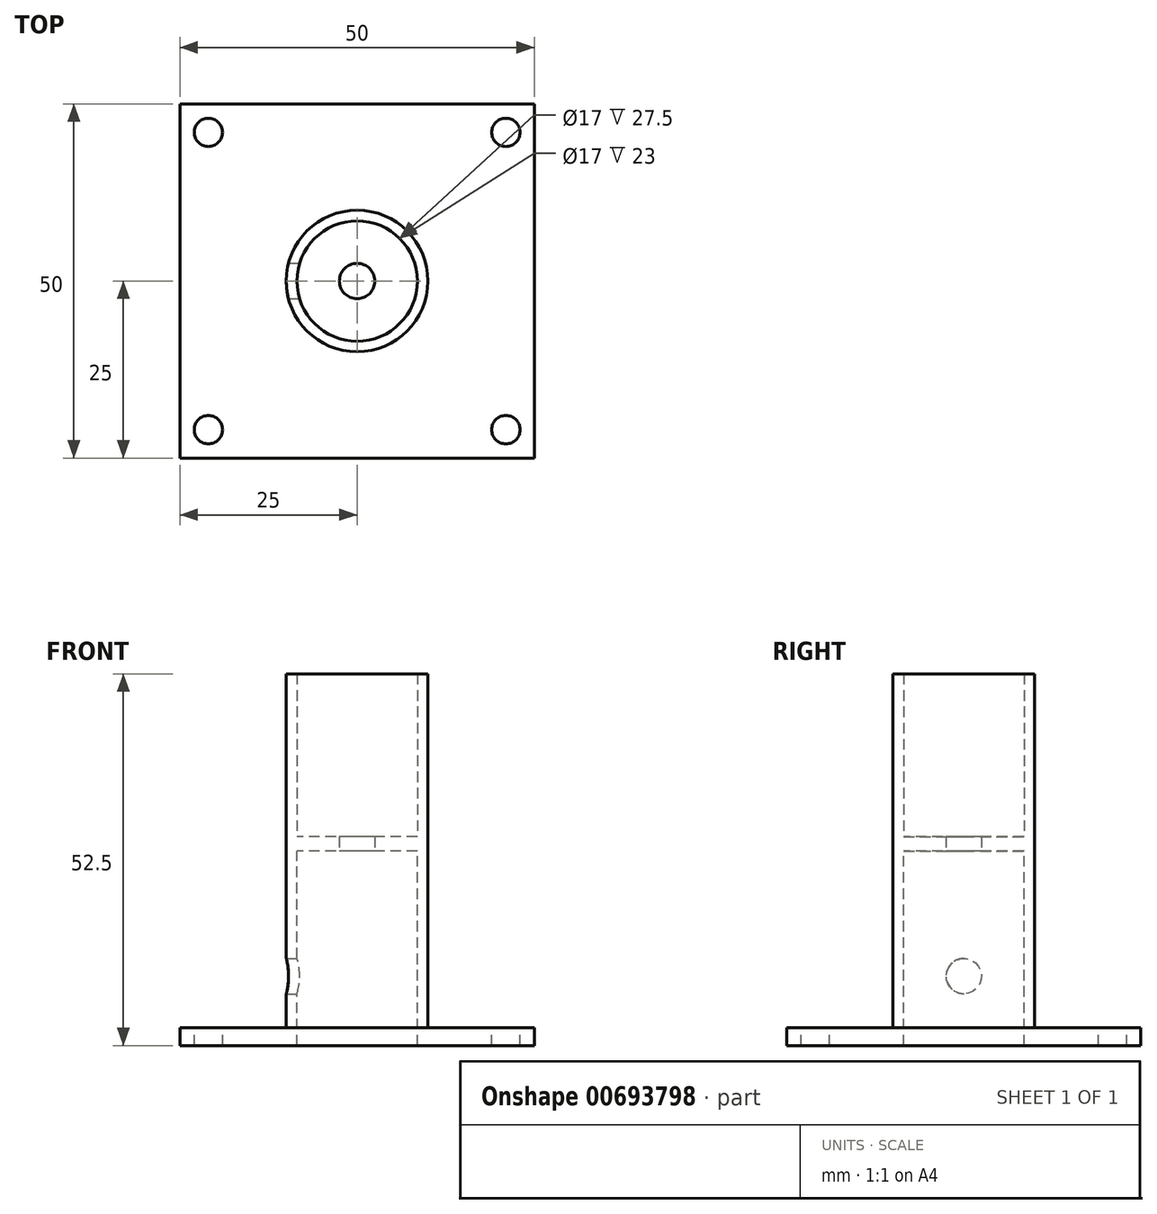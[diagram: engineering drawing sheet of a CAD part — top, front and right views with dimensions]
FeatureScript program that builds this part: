
annotation { "Feature Type Name" : "Feature", "Feature Type Description" : "" }
export const myFeature = defineFeature(function(context is Context, id is Id, definition is map)
    precondition{}
    {
        {
            var Q0;
            Q0=qCreatedBy(makeId("Top.planeOp"),FACE);
            var sketch = newSketch(context, id + "F0", { "sketchPlane" : qUnion([Q0])});
            skLineSegment(sketch, "E0.bottom", {"start": v(-25, 25) * mm, "end": v(25, 25) * mm});
            skLineSegment(sketch, "E0.top", {"start": v(-25, -25) * mm, "end": v(25, -25) * mm});
            skLineSegment(sketch, "E0.left", {"start": v(-25, 25) * mm, "end": v(-25, -25) * mm});
            skLineSegment(sketch, "E0.right", {"start": v(25, 25) * mm, "end": v(25, -25) * mm});
            skPoint(sketch, "E0.middle", {"position": v(0, 0) * mm});
            skCircle(sketch, "E1", {"center": v(0, 0) * mm, "radius": 8.5 * mm});
            skCircle(sketch, "E2", {"center": v(0, 0) * mm, "radius": 10 * mm});
            skLineSegment(sketch, "E3.bottom", {"start": v(21, 21) * mm, "end": v(-21, 21) * mm});
            skLineSegment(sketch, "E3.top", {"start": v(21, -21) * mm, "end": v(-21, -21) * mm});
            skLineSegment(sketch, "E3.left", {"start": v(21, 21) * mm, "end": v(21, -21) * mm});
            skLineSegment(sketch, "E3.right", {"start": v(-21, 21) * mm, "end": v(-21, -21) * mm});
            skCircle(sketch, "E4", {"center": v(-21, 21) * mm, "radius": 2 * mm});
            skCircle(sketch, "E5.MirrorC", {"center": v(21, 21) * mm, "radius": 2 * mm});
            skCircle(sketch, "E6.MirrorC", {"center": v(-21, -21) * mm, "radius": 2 * mm});
            skCircle(sketch, "E7.MirrorC", {"center": v(21, -21) * mm, "radius": 2 * mm});
            skSolve(sketch);
        }
        {
            var Q0;
            Q0 = qSketchRegion(id + "F0", true);
            var Q1;
            Q1=makeQuery(id+"F0.imprint","IMPRINT",FACE,{"disambiguationData":[TD([[makeQuery(id+"F0.imprint","IMPRINT",EDGE,{"derivedFrom":sQuery(id+"F0.wireOp",EDGE,"E2")}),-1.0]])]});
            var Q2;
            Q2=makeQuery(id+"F0.imprint","IMPRINT",FACE,{"disambiguationData":[TD([[makeQuery(id+"F0.imprint","IMPRINT",EDGE,{"derivedFrom":sQuery(id+"F0.wireOp",EDGE,"E1")}),-1.0]])]});
            extrude(context, id + "F1", {"entities" : qUnion([Q0, Q1, Q2]), "oppositeDirection" : true, "depth" : 2.5 * mm, "offsetDistance" : 25 * mm});
        }
        {
            var Q0;
            Q0=makeQuery(id+"F0.imprint","IMPRINT",FACE,{"disambiguationData":[TD([[makeQuery(id+"F0.imprint","IMPRINT",EDGE,{"derivedFrom":sQuery(id+"F0.wireOp",EDGE,"E1")}),-1.0]])]});
            extrude(context, id + "F2", {"entities" : qUnion([Q0]), "operationType" : NewBodyOperationType.ADD, "depth" : 25 * mm, "offsetDistance" : 25 * mm});
        }
        {
            var Q0;
            Q0=makeQuery(id+"F2.opExtrude","CAP_FACE",FACE,{"disambiguationData":[OSD([sQuery(id+"F0.wireOp",EDGE,"E1"),sQuery(id+"F0.wireOp",EDGE,"E2")])],"isStart":false});
            cPlane(context, id + "F3", {"entities" : qUnion([Q0]), "cplaneType" : CPlaneType.OFFSET, "offset" : 0 * mm, "width" : 150 * mm, "height" : 150 * mm});
        }
        {
            var Q0;
            Q0=qCreatedBy(id+"F3.planeOp",FACE);
            var sketch = newSketch(context, id + "F4", { "sketchPlane" : qUnion([Q0])});
            skCircle(sketch, "E8", {"center": v(0, 0) * mm, "radius": 2.5 * mm});
            skCircle(sketch, "E9.0", {"center": v(0, 0) * mm, "radius": 10 * mm});
            skCircle(sketch, "E10.0", {"center": v(0, 0) * mm, "radius": 8.5 * mm});
            skSolve(sketch);
        }
        {
            var Q0;
            Q0=makeQuery(id+"F4.imprint","IMPRINT",FACE,{"disambiguationData":[TD([[makeQuery(id+"F4.imprint","IMPRINT",EDGE,{"derivedFrom":sQuery(id+"F4.wireOp",EDGE,"E8")}),-1.0]])]});
            extrude(context, id + "F5", {"entities" : qUnion([Q0]), "operationType" : NewBodyOperationType.ADD, "depth" : 2 * mm, "offsetDistance" : 25 * mm});
        }
        {
            var Q0;
            Q0=makeQuery(id+"F4.imprint","IMPRINT",FACE,{"disambiguationData":[TD([[makeQuery(id+"F4.imprint","IMPRINT",EDGE,{"derivedFrom":sQuery(id+"F4.wireOp",EDGE,"E9.0")}),1.0]])]});
            extrude(context, id + "F6", {"entities" : qUnion([Q0]), "operationType" : NewBodyOperationType.ADD, "depth" : 25 * mm, "offsetDistance" : 25 * mm});
        }
        {
            var Q0;
            Q0=qCreatedBy(makeId("Right.planeOp"),FACE);
            var sketch = newSketch(context, id + "F7", { "sketchPlane" : qUnion([Q0])});
            skCircle(sketch, "E11", {"center": v(0, 7.3) * mm, "radius": 2.5 * mm});
            skSolve(sketch);
        }
        {
            var Q0;
            Q0=makeQuery(id+"F7.imprint","IMPRINT",FACE,{"disambiguationData":[TD([[makeQuery(id+"F7.imprint","IMPRINT",EDGE,{"derivedFrom":sQuery(id+"F7.wireOp",EDGE,"E11")}),1.0]])]});
            var Q1;
            Q1=sQuery(id+"F7.wireOp",EDGE,"E11");
            extrude(context, id + "F8", {"entities" : qUnion([Q0]), "operationType" : NewBodyOperationType.REMOVE, "surfaceEntities" : qUnion([Q1]), "oppositeDirection" : true, "depth" : 25 * mm, "offsetDistance" : 25 * mm});
        }
    });
